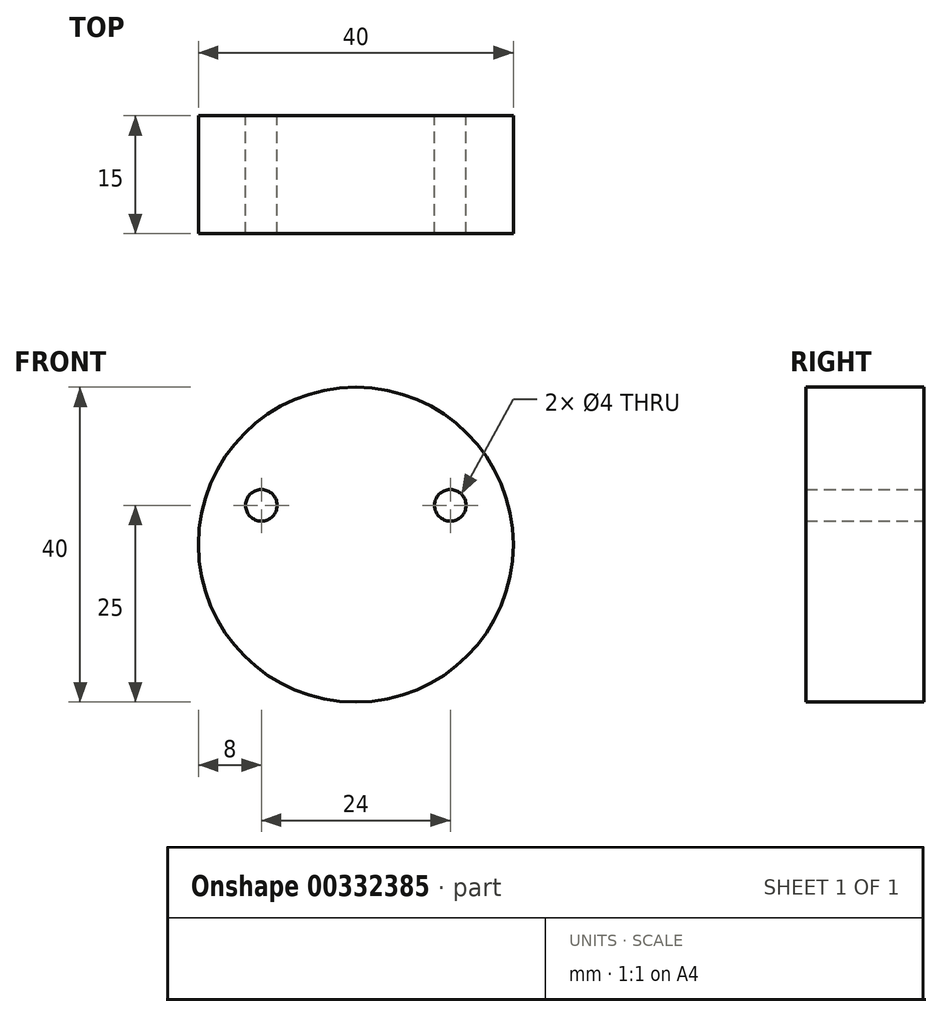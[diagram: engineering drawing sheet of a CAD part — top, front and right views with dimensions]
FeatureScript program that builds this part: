
annotation { "Feature Type Name" : "Feature", "Feature Type Description" : "" }
export const myFeature = defineFeature(function(context is Context, id is Id, definition is map)
    precondition{}
    {
        {
            var Q0;
            Q0=qCreatedBy(makeId("Front.planeOp"),FACE);
            var sketch = newSketch(context, id + "F0", { "sketchPlane" : qUnion([Q0])});
            skCircle(sketch, "E0", {"center": v(0, 0) * mm, "radius": 20 * mm});
            skCircle(sketch, "E1", {"center": v(12, 5) * mm, "radius": 2 * mm});
            skCircle(sketch, "E2", {"center": v(-12, 5) * mm, "radius": 2 * mm});
            skSolve(sketch);
        }
        {
            var Q0;
            Q0=makeQuery(id+"F0.imprint","IMPRINT",FACE,{"disambiguationData":[TD([[makeQuery(id+"F0.imprint","IMPRINT",EDGE,{"derivedFrom":sQuery(id+"F0.wireOp",EDGE,"E0")}),1.0]])]});
            extrude(context, id + "F1", {"entities" : qUnion([Q0]), "depth" : 15 * mm});
        }
    });
